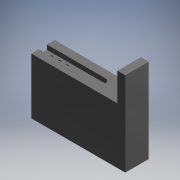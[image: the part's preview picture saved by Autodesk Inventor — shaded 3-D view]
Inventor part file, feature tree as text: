
AUTODESK INVENTOR PART (.ipt)
format: ipt  version: 2019 (Build 230136000, 136)  size: 135,168 bytes
history: native  units: mm (DEFAULTED — no unit token found)
features: sketch x4, extrude x2, hole x2
ambient origin geometry x8: Origin, YZ Plane, XZ Plane, XY Plane, X Axis, Y Axis, Z Axis, Center Point
bodies: Solid1 (feature_tree)
feature tree (8):
  extrude  "Extrusion1"  Depth=68.2498mm
  extrude  "Extrusion2"  Depth=22.86mm
  sketch  "Sketch3"  dims[d4=19.05mm d5=0.0mm d6=47.625mm]
  hole  "Hole1"  [1 undecoded]
  hole  "Hole2"  [1 undecoded]
  sketch  "Sketch1"  dims[d0=76.2mm d1=68.2498mm]
  sketch  "Sketch2"  dims[d2=69.85mm d3=22.86mm]
  sketch  "Sketch4"  dims[d7=6.35mm d8=6.35mm d9=3.7084mm d10=0.0mm d11=6.35mm d12=3.175mm d13=3.175mm d14=3.175mm d15=6.35mm d16=12.7mm d17=19.05mm d18=19.05mm d19=9.525mm d20=9.525mm d21=6.35mm d22=6.35mm d23=2.6416mm d24=7.112mm d25=9.525mm d26=6.35mm d27=14.3117mm d28=7.112mm d29=20.594885mm d30=2.6416mm d31=7.112mm d32=9.525mm d33=6.35mm d34=14.3117mm d35=7.112mm d36=20.594885mm]
note: 2 required parameter values undecoded (feature->parameter linkage not recoverable at this tier; creation-order binding heuristic only, values carry confidence <= 0.55)
